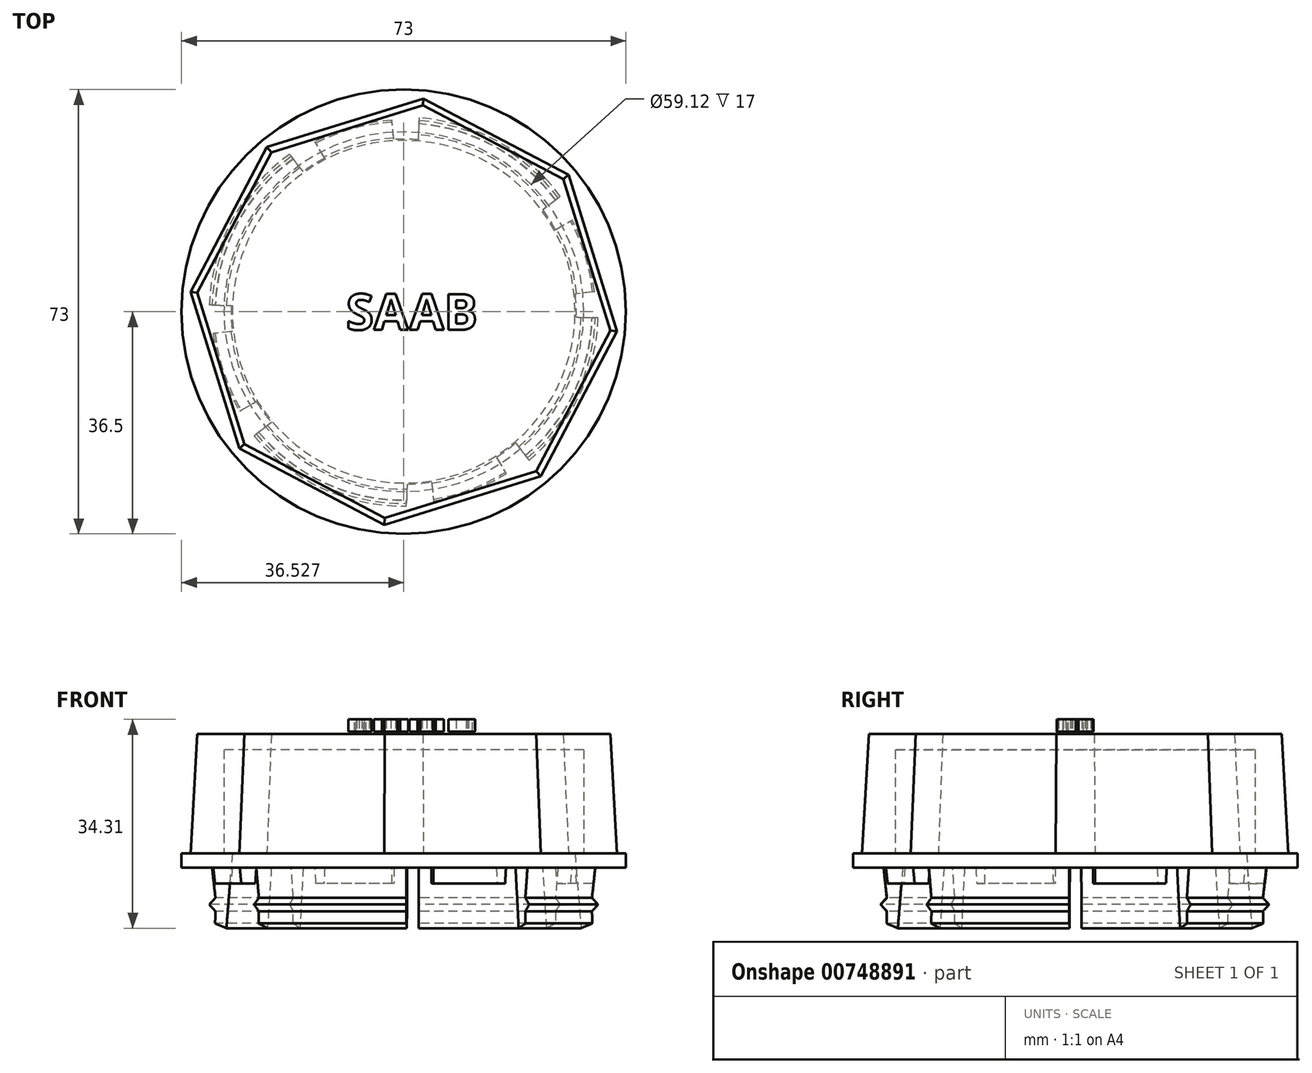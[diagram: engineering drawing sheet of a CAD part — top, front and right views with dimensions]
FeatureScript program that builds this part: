
annotation { "Feature Type Name" : "Feature", "Feature Type Description" : "" }
export const myFeature = defineFeature(function(context is Context, id is Id, definition is map)
    precondition{}
    {
        {
            var Q0;
            Q0=qCreatedBy(makeId("Top.planeOp"),FACE);
            var sketch = newSketch(context, id + "F0", { "sketchPlane" : qUnion([Q0])});
            skCircle(sketch, "E0.cCircle", {"center": v(41.88, 0) * mm, "radius": 35.18 * mm, "construction": true});
            skLineSegment(sketch, "E0.0", {"start": v(14.82, -22.49) * mm, "end": v(6.85, 3.23) * mm});
            skLineSegment(sketch, "E0.1", {"start": v(6.85, 3.23) * mm, "end": v(19.39, 27.05) * mm});
            skLineSegment(sketch, "E0.2", {"start": v(19.39, 27.05) * mm, "end": v(45.1, 35.03) * mm});
            skLineSegment(sketch, "E0.3", {"start": v(45.1, 35.03) * mm, "end": v(68.93, 22.49) * mm});
            skLineSegment(sketch, "E0.4", {"start": v(68.93, 22.49) * mm, "end": v(76.9, -3.23) * mm});
            skLineSegment(sketch, "E0.5", {"start": v(76.9, -3.23) * mm, "end": v(64.36, -27.05) * mm});
            skLineSegment(sketch, "E0.6", {"start": v(64.36, -27.05) * mm, "end": v(38.65, -35.03) * mm});
            skLineSegment(sketch, "E0.7", {"start": v(38.65, -35.03) * mm, "end": v(14.82, -22.49) * mm});
            skSolve(sketch);
        }
        {
            var Q0;
            Q0=qSketchRegion(id+"F0",true);
            extrude(context, id + "F1", {"entities" : qUnion([Q0]), "depth" : 19.6 * mm, "offsetDistance" : 25 * mm, "hasDraft" : true, "draftAngle" : 3 * degree, "draftPullDirection" : true});
        }
        {
            var Q0;
            Q0=qCreatedBy(makeId("Front.planeOp"),FACE);
            var sketch = newSketch(context, id + "F2", { "sketchPlane" : qUnion([Q0])});
            skLineSegment(sketch, "E1", {"start": v(71.3, 19.61) * mm, "end": v(71.3, 20.31) * mm});
            skLineSegment(sketch, "E2", {"start": v(71.3, 20.31) * mm, "end": v(70.7, 20.31) * mm});
            skLineSegment(sketch, "E3", {"start": v(70.7, 20.31) * mm, "end": v(70.7, 19.61) * mm});
            skLineSegment(sketch, "E4", {"start": v(61.4, 22) * mm, "end": v(61.4, 21.36) * mm});
            skLineSegment(sketch, "E5", {"start": v(61.4, 21.36) * mm, "end": v(41.94, 21.36) * mm});
            skArc(sketch, "E6", {"start": v(70.7, 19.61) * mm, "mid": v(66.19, 21.38) * mm, "end": v(61.4, 22) * mm});
            skLineSegment(sketch, "E7", {"start": v(41.94, 21.36) * mm, "end": v(41.94, 19.6) * mm});
            skSolve(sketch);
        }
        {
            var Q0;
            Q0=qSketchRegion(id+"F2",true);
            var Q1;
            Q1=sQuery(id+"F2.wireOp",EDGE,"E5");
            var Q2;
            Q2=sQuery(id+"F2.wireOp",EDGE,"E4");
            var Q3;
            Q3=sQuery(id+"F2.wireOp",EDGE,"E6");
            var Q4;
            Q4=sQuery(id+"F2.wireOp",EDGE,"E1");
            var Q5;
            Q5=sQuery(id+"F2.wireOp",EDGE,"E3");
            var Q6;
            Q6=sQuery(id+"F2.wireOp",EDGE,"E2");
            var Q7;
            Q7=sQuery(id+"F2.wireOp",EDGE,"E7");
            revolve(context, id + "F3", {"bodyType" : ToolBodyType.SURFACE, "surfaceOperationType" : NewSurfaceOperationType.NEW, "entities" : qUnion([Q0]), "surfaceEntities" : qUnion([Q1, Q2, Q3, Q4, Q5, Q6]), "axis" : qUnion([Q7]), "revolveType" : RevolveType.FULL});
        }
        {
            var Q0;
            Q0=qCreatedBy(makeId("Front.planeOp"),FACE);
            var sketch = newSketch(context, id + "F4", { "sketchPlane" : qUnion([Q0])});
            skLineSegment(sketch, "E8", {"start": v(41.85, 2.47) * mm, "end": v(41.85, -0.28) * mm});
            skLineSegment(sketch, "E9", {"start": v(13.92, 0) * mm, "end": v(10.66, 0) * mm});
            skLineSegment(sketch, "E10", {"start": v(13.7, 0) * mm, "end": v(12.7, -12.3) * mm});
            skLineSegment(sketch, "E11", {"start": v(12.7, -12.3) * mm, "end": v(10.85, -11.54) * mm});
            skLineSegment(sketch, "E12", {"start": v(10.85, -11.54) * mm, "end": v(10.9, -9.54) * mm});
            skLineSegment(sketch, "E13", {"start": v(9.9, -8.43) * mm, "end": v(10.9, -9.54) * mm});
            skLineSegment(sketch, "E14", {"start": v(9.9, -8.43) * mm, "end": v(10.9, -7.32) * mm});
            skLineSegment(sketch, "E15", {"start": v(10.9, -7.32) * mm, "end": v(10.35, -2.35) * mm});
            skLineSegment(sketch, "E16", {"start": v(41.85, 0) * mm, "end": v(5.35, 0) * mm});
            skLineSegment(sketch, "E17", {"start": v(41.85, 2.47) * mm, "end": v(41.85, -22.81) * mm});
            skPoint(sketch, "E18", {"position": v(5.35, -2.35) * mm});
            skLineSegment(sketch, "E19", {"start": v(5.35, -2.35) * mm, "end": v(10.35, -2.35) * mm});
            skLineSegment(sketch, "E20", {"start": v(5.35, 0) * mm, "end": v(5.35, -2.35) * mm});
            skPoint(sketch, "E21", {"position": v(10.85, 0) * mm});
            skSolve(sketch);
        }
        {
            var Q0;
            Q0=qSketchRegion(id+"F4",true);
            var Q1;
            Q1=sQuery(id+"F4.wireOp",EDGE,"E16");
            var Q2;
            Q2=sQuery(id+"F4.wireOp",EDGE,"4cd7ZZWE-5ar5-vtm7-FDXw-HXyrbe5Stu3w");
            var Q3;
            Q3=sQuery(id+"F4.wireOp",EDGE,"E15");
            var Q4;
            Q4=sQuery(id+"F4.wireOp",EDGE,"E14");
            var Q5;
            Q5=sQuery(id+"F4.wireOp",EDGE,"E13");
            var Q6;
            Q6=sQuery(id+"F4.wireOp",EDGE,"E11");
            var Q7;
            Q7=sQuery(id+"F4.wireOp",EDGE,"E12");
            var Q8;
            Q8=sQuery(id+"F4.wireOp",EDGE,"E10");
            var Q9;
            Q9=sQuery(id+"F4.wireOp",EDGE,"E17");
            revolve(context, id + "F5", {"surfaceOperationType" : NewSurfaceOperationType.NEW, "entities" : qUnion([Q0]), "surfaceEntities" : qUnion([Q1, Q2, Q3, Q4, Q5, Q6, Q7, Q8]), "axis" : qUnion([Q9]), "revolveType" : RevolveType.FULL});
        }
        {
            var Q0;
            Q0=qCreatedBy(makeId("Top.planeOp"),FACE);
            var sketch = newSketch(context, id + "F6", { "sketchPlane" : qUnion([Q0])});
            skCircle(sketch, "E22", {"center": v(41.88, 0) * mm, "radius": 29.56 * mm});
            skSolve(sketch);
        }
        {
            var Q0;
            Q0=qSketchRegion(id+"F6",true);
            extrude(context, id + "F7", {"entities" : qUnion([Q0]), "operationType" : NewBodyOperationType.REMOVE, "depth" : 17 * mm, "offsetDistance" : 25 * mm});
        }
        {
            var Q0;
            Q0=qCreatedBy(makeId("Top.planeOp"),FACE);
            var sketch = newSketch(context, id + "F8", { "sketchPlane" : qUnion([Q0])});
            skText(sketch, "E23", { "text": "SAAB", "fontName": "OpenSans-Bold.ttf"});
            const initialGuessF8  = {"E23": [0.03239, -0.00298, 1, 0, 0.00593]};
            skSetInitialGuess(sketch, initialGuessF8);
            skSolve(sketch);
        }
        {
            var Q0;
            Q0=qSketchRegion(id+"F8",true);
            extrude(context, id + "F9", {"entities" : qUnion([Q0]), "depth" : 2 * mm, "offsetDistance" : 25 * mm});
        }
        {
            var Q0;
            Q0=makeQuery(id+"F9.opExtrude","SWEPT_BODY",BODY,{"disambiguationData":[OSD([sQuery(id+"F8.wireOp",EDGE,"E23.sketch_text.stroke-0"),sQuery(id+"F8.wireOp",EDGE,"E23.sketch_text.stroke-1"),sQuery(id+"F8.wireOp",EDGE,"E23.sketch_text.stroke-2"),sQuery(id+"F8.wireOp",EDGE,"E23.sketch_text.stroke-3"),sQuery(id+"F8.wireOp",EDGE,"E23.sketch_text.stroke-4"),sQuery(id+"F8.wireOp",EDGE,"E23.sketch_text.stroke-5"),sQuery(id+"F8.wireOp",EDGE,"E23.sketch_text.stroke-6"),sQuery(id+"F8.wireOp",EDGE,"E23.sketch_text.stroke-7"),sQuery(id+"F8.wireOp",EDGE,"E23.sketch_text.stroke-8"),sQuery(id+"F8.wireOp",EDGE,"E23.sketch_text.stroke-9"),sQuery(id+"F8.wireOp",EDGE,"E23.sketch_text.stroke-10"),sQuery(id+"F8.wireOp",EDGE,"E23.sketch_text.stroke-11"),sQuery(id+"F8.wireOp",EDGE,"E23.sketch_text.stroke-12"),sQuery(id+"F8.wireOp",EDGE,"E23.sketch_text.stroke-13"),sQuery(id+"F8.wireOp",EDGE,"E23.sketch_text.stroke-14"),sQuery(id+"F8.wireOp",EDGE,"E23.sketch_text.stroke-15"),sQuery(id+"F8.wireOp",EDGE,"E23.sketch_text.stroke-16"),sQuery(id+"F8.wireOp",EDGE,"E23.sketch_text.stroke-17"),sQuery(id+"F8.wireOp",EDGE,"E23.sketch_text.stroke-18"),sQuery(id+"F8.wireOp",EDGE,"E23.sketch_text.stroke-19"),sQuery(id+"F8.wireOp",EDGE,"E23.sketch_text.stroke-20"),sQuery(id+"F8.wireOp",EDGE,"E23.sketch_text.stroke-21"),sQuery(id+"F8.wireOp",EDGE,"E23.sketch_text.stroke-22"),sQuery(id+"F8.wireOp",EDGE,"E23.sketch_text.stroke-23"),sQuery(id+"F8.wireOp",EDGE,"E23.sketch_text.stroke-24"),sQuery(id+"F8.wireOp",EDGE,"E23.sketch_text.stroke-25"),sQuery(id+"F8.wireOp",EDGE,"E23.sketch_text.stroke-26"),sQuery(id+"F8.wireOp",EDGE,"E23.sketch_text.stroke-27")])]});
            var Q1;
            Q1=makeQuery(id+"F9.opExtrude","SWEPT_BODY",BODY,{"disambiguationData":[OSD([sQuery(id+"F8.wireOp",EDGE,"E23.sketch_text.stroke-28"),sQuery(id+"F8.wireOp",EDGE,"E23.sketch_text.stroke-29"),sQuery(id+"F8.wireOp",EDGE,"E23.sketch_text.stroke-30"),sQuery(id+"F8.wireOp",EDGE,"E23.sketch_text.stroke-31"),sQuery(id+"F8.wireOp",EDGE,"E23.sketch_text.stroke-32"),sQuery(id+"F8.wireOp",EDGE,"E23.sketch_text.stroke-33"),sQuery(id+"F8.wireOp",EDGE,"E23.sketch_text.stroke-34"),sQuery(id+"F8.wireOp",EDGE,"E23.sketch_text.stroke-35"),sQuery(id+"F8.wireOp",EDGE,"E23.sketch_text.stroke-36"),sQuery(id+"F8.wireOp",EDGE,"E23.sketch_text.stroke-37"),sQuery(id+"F8.wireOp",EDGE,"E23.sketch_text.stroke-38"),sQuery(id+"F8.wireOp",EDGE,"E23.sketch_text.stroke-39")])]});
            var Q2;
            Q2=makeQuery(id+"F9.opExtrude","SWEPT_BODY",BODY,{"disambiguationData":[OSD([sQuery(id+"F8.wireOp",EDGE,"E23.sketch_text.stroke-40"),sQuery(id+"F8.wireOp",EDGE,"E23.sketch_text.stroke-41"),sQuery(id+"F8.wireOp",EDGE,"E23.sketch_text.stroke-42"),sQuery(id+"F8.wireOp",EDGE,"E23.sketch_text.stroke-43"),sQuery(id+"F8.wireOp",EDGE,"E23.sketch_text.stroke-44"),sQuery(id+"F8.wireOp",EDGE,"E23.sketch_text.stroke-45"),sQuery(id+"F8.wireOp",EDGE,"E23.sketch_text.stroke-46"),sQuery(id+"F8.wireOp",EDGE,"E23.sketch_text.stroke-47"),sQuery(id+"F8.wireOp",EDGE,"E23.sketch_text.stroke-48"),sQuery(id+"F8.wireOp",EDGE,"E23.sketch_text.stroke-49"),sQuery(id+"F8.wireOp",EDGE,"E23.sketch_text.stroke-50"),sQuery(id+"F8.wireOp",EDGE,"E23.sketch_text.stroke-51")])]});
            var Q3;
            Q3=makeQuery(id+"F9.opExtrude","SWEPT_BODY",BODY,{"disambiguationData":[OSD([sQuery(id+"F8.wireOp",EDGE,"E23.sketch_text.stroke-52"),sQuery(id+"F8.wireOp",EDGE,"E23.sketch_text.stroke-53"),sQuery(id+"F8.wireOp",EDGE,"E23.sketch_text.stroke-54"),sQuery(id+"F8.wireOp",EDGE,"E23.sketch_text.stroke-55"),sQuery(id+"F8.wireOp",EDGE,"E23.sketch_text.stroke-56"),sQuery(id+"F8.wireOp",EDGE,"E23.sketch_text.stroke-57"),sQuery(id+"F8.wireOp",EDGE,"E23.sketch_text.stroke-58"),sQuery(id+"F8.wireOp",EDGE,"E23.sketch_text.stroke-59"),sQuery(id+"F8.wireOp",EDGE,"E23.sketch_text.stroke-60"),sQuery(id+"F8.wireOp",EDGE,"E23.sketch_text.stroke-61"),sQuery(id+"F8.wireOp",EDGE,"E23.sketch_text.stroke-62"),sQuery(id+"F8.wireOp",EDGE,"E23.sketch_text.stroke-63"),sQuery(id+"F8.wireOp",EDGE,"E23.sketch_text.stroke-64"),sQuery(id+"F8.wireOp",EDGE,"E23.sketch_text.stroke-65"),sQuery(id+"F8.wireOp",EDGE,"E23.sketch_text.stroke-66"),sQuery(id+"F8.wireOp",EDGE,"E23.sketch_text.stroke-67"),sQuery(id+"F8.wireOp",EDGE,"E23.sketch_text.stroke-68"),sQuery(id+"F8.wireOp",EDGE,"E23.sketch_text.stroke-69"),sQuery(id+"F8.wireOp",EDGE,"E23.sketch_text.stroke-70"),sQuery(id+"F8.wireOp",EDGE,"E23.sketch_text.stroke-71"),sQuery(id+"F8.wireOp",EDGE,"E23.sketch_text.stroke-72"),sQuery(id+"F8.wireOp",EDGE,"E23.sketch_text.stroke-73"),sQuery(id+"F8.wireOp",EDGE,"E23.sketch_text.stroke-74"),sQuery(id+"F8.wireOp",EDGE,"E23.sketch_text.stroke-75"),sQuery(id+"F8.wireOp",EDGE,"E23.sketch_text.stroke-76")])]});
            transform(context, id + "F10", {"entities" : qUnion([Q0, Q1, Q2, Q3]), "transformType" : TransformType.TRANSLATION_3D, "dx" : 0 * mm, "dy" : 0 * mm, "dz" : 20 * mm, "makeCopy" : false});
        }
        {
            var Q0;
            Q0=qCreatedBy(makeId("Top.planeOp"),FACE);
            var sketch = newSketch(context, id + "F11", { "sketchPlane" : qUnion([Q0])});
            skLineSegment(sketch, "E24", {"start": v(69.85, -34.13) * mm, "end": v(16.32, 34.78) * mm});
            skLineSegment(sketch, "E25", {"start": v(16.32, 34.78) * mm, "end": v(43.91, 43.26) * mm});
            skLineSegment(sketch, "E26", {"start": v(43.91, 43.26) * mm, "end": v(42.61, -43.16) * mm});
            skLineSegment(sketch, "E27", {"start": v(9.14, -26.59) * mm, "end": v(79.03, 27.7) * mm});
            skLineSegment(sketch, "E28", {"start": v(79.03, 27.7) * mm, "end": v(86.57, -0.61) * mm});
            skLineSegment(sketch, "E29", {"start": v(86.57, -0.61) * mm, "end": v(43.22, 0) * mm});
            skLineSegment(sketch, "E30", {"start": v(42.61, -43.16) * mm, "end": v(69.85, -34.13) * mm});
            skLineSegment(sketch, "E31", {"start": v(0, 0.68) * mm, "end": v(43.22, 0) * mm});
            skLineSegment(sketch, "E32", {"start": v(9.14, -26.59) * mm, "end": v(0, 0.68) * mm});
            skPoint(sketch, "E33", {"position": v(19.48, -18.55) * mm});
            skPoint(sketch, "E34", {"position": v(12.6, 0.48) * mm});
            skPoint(sketch, "E35", {"position": v(24.83, 23.83) * mm});
            skPoint(sketch, "E36", {"position": v(42.83, -28.88) * mm});
            skPoint(sketch, "E37", {"position": v(60.43, -22) * mm});
            skPoint(sketch, "E38", {"position": v(71.17, -0.4) * mm});
            skPoint(sketch, "E39", {"position": v(65.22, 16.98) * mm});
            skPoint(sketch, "E40", {"position": v(43.69, 28.4) * mm});
            skLineSegment(sketch, "E41", {"start": v(12.6, 0.48) * mm, "end": v(19.48, -18.55) * mm});
            skLineSegment(sketch, "E42", {"start": v(24.83, 23.83) * mm, "end": v(43.69, 28.4) * mm});
            skLineSegment(sketch, "E43", {"start": v(65.22, 16.98) * mm, "end": v(71.17, -0.4) * mm});
            skLineSegment(sketch, "E44", {"start": v(60.43, -22) * mm, "end": v(42.83, -28.88) * mm});
            skSolve(sketch);
        }
        {
            var Q0;
            Q0 = qSketchRegion(id + "F11", true);
            extrude(context, id + "F12", {"entities" : qUnion([Q0]), "oppositeDirection" : true, "depth" : 25 * mm, "offsetDistance" : 25 * mm, "hasSecondDirection" : true, "secondDirectionOppositeDirection" : true, "secondDirectionDepth" : 5 * mm});
        }
        {
            var Q0;
            Q0=makeQuery(id+"F12.opExtrude","SWEPT_BODY",BODY,{"disambiguationData":[OSD([sQuery(id+"F11.wireOp",EDGE,"E24"),sQuery(id+"F11.wireOp",EDGE,"E26"),sQuery(id+"F11.wireOp",EDGE,"E27"),sQuery(id+"F11.wireOp",EDGE,"E29"),sQuery(id+"F11.wireOp",EDGE,"E30"),sQuery(id+"F11.wireOp",EDGE,"E31"),sQuery(id+"F11.wireOp",EDGE,"E32")])]});
            var Q1;
            Q1=makeQuery(id+"F12.opExtrude","SWEPT_BODY",BODY,{"disambiguationData":[OSD([sQuery(id+"F11.wireOp",EDGE,"E27"),sQuery(id+"F11.wireOp",EDGE,"E28"),sQuery(id+"F11.wireOp",EDGE,"E29")])]});
            var Q2;
            Q2=makeQuery(id+"F12.opExtrude","SWEPT_BODY",BODY,{"disambiguationData":[OSD([sQuery(id+"F11.wireOp",EDGE,"E24"),sQuery(id+"F11.wireOp",EDGE,"E25"),sQuery(id+"F11.wireOp",EDGE,"E26")])]});
            var Q3;
            Q3=makeQuery(id+"FadKjfFnsJpzDV8_9.opBoolean","SPLIT",BODY,{"disambiguationData":[OD(5.0)],"derivedFrom":makeQuery(id+"F5.opRevolve","SWEPT_BODY",BODY,{"disambiguationData":[OSD([sQuery(id+"F4.wireOp",EDGE,"E10"),sQuery(id+"F4.wireOp",EDGE,"E11"),sQuery(id+"F4.wireOp",EDGE,"E12"),sQuery(id+"F4.wireOp",EDGE,"E13"),sQuery(id+"F4.wireOp",EDGE,"E14"),sQuery(id+"F4.wireOp",EDGE,"E15"),sQuery(id+"F4.wireOp",EDGE,"E16"),sQuery(id+"F4.wireOp",EDGE,"E19"),sQuery(id+"F4.wireOp",EDGE,"E20")])]})});
            var Q4;
            Q4=makeQuery(id+"FadKjfFnsJpzDV8_9.opBoolean","SPLIT",BODY,{"disambiguationData":[OD(3.0)],"derivedFrom":makeQuery(id+"F5.opRevolve","SWEPT_BODY",BODY,{"disambiguationData":[OSD([sQuery(id+"F4.wireOp",EDGE,"E10"),sQuery(id+"F4.wireOp",EDGE,"E11"),sQuery(id+"F4.wireOp",EDGE,"E12"),sQuery(id+"F4.wireOp",EDGE,"E13"),sQuery(id+"F4.wireOp",EDGE,"E14"),sQuery(id+"F4.wireOp",EDGE,"E15"),sQuery(id+"F4.wireOp",EDGE,"E16"),sQuery(id+"F4.wireOp",EDGE,"E19"),sQuery(id+"F4.wireOp",EDGE,"E20")])]})});
            var Q5;
            Q5=makeQuery(id+"FadKjfFnsJpzDV8_9.opBoolean","SPLIT",BODY,{"disambiguationData":[OD(7.0)],"derivedFrom":makeQuery(id+"F5.opRevolve","SWEPT_BODY",BODY,{"disambiguationData":[OSD([sQuery(id+"F4.wireOp",EDGE,"E10"),sQuery(id+"F4.wireOp",EDGE,"E11"),sQuery(id+"F4.wireOp",EDGE,"E12"),sQuery(id+"F4.wireOp",EDGE,"E13"),sQuery(id+"F4.wireOp",EDGE,"E14"),sQuery(id+"F4.wireOp",EDGE,"E15"),sQuery(id+"F4.wireOp",EDGE,"E16"),sQuery(id+"F4.wireOp",EDGE,"E19"),sQuery(id+"F4.wireOp",EDGE,"E20")])]})});
            var Q6;
            Q6=makeQuery(id+"FadKjfFnsJpzDV8_9.opBoolean","SPLIT",BODY,{"disambiguationData":[OD(2.0)],"derivedFrom":makeQuery(id+"F5.opRevolve","SWEPT_BODY",BODY,{"disambiguationData":[OSD([sQuery(id+"F4.wireOp",EDGE,"E10"),sQuery(id+"F4.wireOp",EDGE,"E11"),sQuery(id+"F4.wireOp",EDGE,"E12"),sQuery(id+"F4.wireOp",EDGE,"E13"),sQuery(id+"F4.wireOp",EDGE,"E14"),sQuery(id+"F4.wireOp",EDGE,"E15"),sQuery(id+"F4.wireOp",EDGE,"E16"),sQuery(id+"F4.wireOp",EDGE,"E19"),sQuery(id+"F4.wireOp",EDGE,"E20")])]})});
            var Q7;
            Q7=makeQuery(id+"FadKjfFnsJpzDV8_9.opBoolean","SPLIT",BODY,{"disambiguationData":[OD(0.0)],"derivedFrom":makeQuery(id+"F5.opRevolve","SWEPT_BODY",BODY,{"disambiguationData":[OSD([sQuery(id+"F4.wireOp",EDGE,"E10"),sQuery(id+"F4.wireOp",EDGE,"E11"),sQuery(id+"F4.wireOp",EDGE,"E12"),sQuery(id+"F4.wireOp",EDGE,"E13"),sQuery(id+"F4.wireOp",EDGE,"E14"),sQuery(id+"F4.wireOp",EDGE,"E15"),sQuery(id+"F4.wireOp",EDGE,"E16"),sQuery(id+"F4.wireOp",EDGE,"E19"),sQuery(id+"F4.wireOp",EDGE,"E20")])]})});
            var Q8;
            Q8=makeQuery(id+"FadKjfFnsJpzDV8_9.opBoolean","SPLIT",BODY,{"disambiguationData":[OD(6.0)],"derivedFrom":makeQuery(id+"F5.opRevolve","SWEPT_BODY",BODY,{"disambiguationData":[OSD([sQuery(id+"F4.wireOp",EDGE,"E10"),sQuery(id+"F4.wireOp",EDGE,"E11"),sQuery(id+"F4.wireOp",EDGE,"E12"),sQuery(id+"F4.wireOp",EDGE,"E13"),sQuery(id+"F4.wireOp",EDGE,"E14"),sQuery(id+"F4.wireOp",EDGE,"E15"),sQuery(id+"F4.wireOp",EDGE,"E16"),sQuery(id+"F4.wireOp",EDGE,"E19"),sQuery(id+"F4.wireOp",EDGE,"E20")])]})});
            var Q9;
            Q9=makeQuery(id+"FadKjfFnsJpzDV8_9.opBoolean","SPLIT",BODY,{"disambiguationData":[OD(4.0)],"derivedFrom":makeQuery(id+"F5.opRevolve","SWEPT_BODY",BODY,{"disambiguationData":[OSD([sQuery(id+"F4.wireOp",EDGE,"E10"),sQuery(id+"F4.wireOp",EDGE,"E11"),sQuery(id+"F4.wireOp",EDGE,"E12"),sQuery(id+"F4.wireOp",EDGE,"E13"),sQuery(id+"F4.wireOp",EDGE,"E14"),sQuery(id+"F4.wireOp",EDGE,"E15"),sQuery(id+"F4.wireOp",EDGE,"E16"),sQuery(id+"F4.wireOp",EDGE,"E19"),sQuery(id+"F4.wireOp",EDGE,"E20")])]})});
            var Q10;
            Q10=makeQuery(id+"FadKjfFnsJpzDV8_9.opBoolean","SPLIT",BODY,{"disambiguationData":[OD(1.0)],"derivedFrom":makeQuery(id+"F5.opRevolve","SWEPT_BODY",BODY,{"disambiguationData":[OSD([sQuery(id+"F4.wireOp",EDGE,"E10"),sQuery(id+"F4.wireOp",EDGE,"E11"),sQuery(id+"F4.wireOp",EDGE,"E12"),sQuery(id+"F4.wireOp",EDGE,"E13"),sQuery(id+"F4.wireOp",EDGE,"E14"),sQuery(id+"F4.wireOp",EDGE,"E15"),sQuery(id+"F4.wireOp",EDGE,"E16"),sQuery(id+"F4.wireOp",EDGE,"E19"),sQuery(id+"F4.wireOp",EDGE,"E20")])]})});
            booleanBodies(context, id + "F13", {"operationType" : BooleanOperationType.SUBTRACTION, "tools" : qUnion([Q0, Q1, Q2]), "targets" : qUnion([Q3, Q4, Q5, Q6, Q7, Q8, Q9, Q10])});
        }
        {
            var Q0;
            Q0=qCreatedBy(makeId("Top.planeOp"),FACE);
            var sketch = newSketch(context, id + "F14", { "sketchPlane" : qUnion([Q0])});
            skPoint(sketch, "E45.endSnap0", {"position": v(222.12, 4.24) * mm});
            skPoint(sketch, "E46", {"position": v(43.35, 0) * mm});
            skLineSegment(sketch, "E47", {"start": v(76.6, 26.03) * mm, "end": v(5.98, -29.26) * mm});
            skLineSegment(sketch, "E48", {"start": v(43.35, 0) * mm, "end": v(74.1, -39.28) * mm});
            skLineSegment(sketch, "E49", {"start": v(43.35, 0) * mm, "end": v(14.72, 36.58) * mm});
            skLineSegment(sketch, "E50", {"start": v(1.61, -23.99) * mm, "end": v(43.35, 0) * mm});
            skLineSegment(sketch, "E51", {"start": v(43.35, 0) * mm, "end": v(69.77, -45.97) * mm});
            skLineSegment(sketch, "E52", {"start": v(43.35, 0) * mm, "end": v(81.27, 21.79) * mm});
            skLineSegment(sketch, "E53", {"start": v(43.35, 0) * mm, "end": v(20.03, 40.59) * mm});
            skLineSegment(sketch, "E54", {"start": v(14.72, 36.58) * mm, "end": v(20.03, 40.59) * mm});
            skLineSegment(sketch, "E55", {"start": v(76.6, 26.03) * mm, "end": v(81.27, 21.79) * mm});
            skLineSegment(sketch, "E56", {"start": v(74.1, -39.28) * mm, "end": v(69.77, -45.97) * mm});
            skLineSegment(sketch, "E57", {"start": v(5.98, -29.26) * mm, "end": v(1.61, -23.99) * mm});
            skLineSegment(sketch, "E58", {"start": v(85.32, 4.6) * mm, "end": v(-3.82, -5.18) * mm});
            skLineSegment(sketch, "E59", {"start": v(43.35, 0) * mm, "end": v(48.8, -49.6) * mm});
            skLineSegment(sketch, "E60", {"start": v(43.35, 0) * mm, "end": v(38.29, 46.18) * mm});
            skLineSegment(sketch, "E61", {"start": v(-4.76, 1.6) * mm, "end": v(43.35, 0) * mm});
            skLineSegment(sketch, "E62", {"start": v(43.35, 0) * mm, "end": v(41.59, -52.99) * mm});
            skLineSegment(sketch, "E63", {"start": v(43.35, 0) * mm, "end": v(87.06, -1.46) * mm});
            skLineSegment(sketch, "E64", {"start": v(43.35, 0) * mm, "end": v(44.92, 46.79) * mm});
            skLineSegment(sketch, "E65", {"start": v(38.29, 46.18) * mm, "end": v(44.92, 46.79) * mm});
            skLineSegment(sketch, "E66", {"start": v(85.32, 4.6) * mm, "end": v(87.06, -1.46) * mm});
            skLineSegment(sketch, "E67", {"start": v(48.8, -49.6) * mm, "end": v(41.59, -52.99) * mm});
            skLineSegment(sketch, "E68", {"start": v(-3.82, -5.18) * mm, "end": v(-4.76, 1.6) * mm});
            skSolve(sketch);
        }
        {
            var Q0;
            Q0 = qSketchRegion(id + "F14", true);
            extrude(context, id + "F15", {"entities" : qUnion([Q0]), "oppositeDirection" : true, "depth" : 10 * mm, "offsetDistance" : 25 * mm});
        }
        {
            var Q0;
            Q0=makeQuery(id+"F15.opExtrude","SWEPT_BODY",BODY,{"disambiguationData":[OSD([sQuery(id+"F14.wireOp",EDGE,"E49"),sQuery(id+"F14.wireOp",EDGE,"E53"),sQuery(id+"F14.wireOp",EDGE,"E54")])]});
            var Q1;
            Q1=makeQuery(id+"F15.opExtrude","SWEPT_BODY",BODY,{"disambiguationData":[OSD([sQuery(id+"F14.wireOp",EDGE,"E58"),sQuery(id+"F14.wireOp",EDGE,"E61"),sQuery(id+"F14.wireOp",EDGE,"E68")])]});
            var Q2;
            Q2=makeQuery(id+"F15.opExtrude","SWEPT_BODY",BODY,{"disambiguationData":[OSD([sQuery(id+"F14.wireOp",EDGE,"E47"),sQuery(id+"F14.wireOp",EDGE,"E50"),sQuery(id+"F14.wireOp",EDGE,"E57")])]});
            var Q3;
            Q3=makeQuery(id+"F15.opExtrude","SWEPT_BODY",BODY,{"disambiguationData":[OSD([sQuery(id+"F14.wireOp",EDGE,"E59"),sQuery(id+"F14.wireOp",EDGE,"E62"),sQuery(id+"F14.wireOp",EDGE,"E67")])]});
            var Q4;
            Q4=makeQuery(id+"F15.opExtrude","SWEPT_BODY",BODY,{"disambiguationData":[OSD([sQuery(id+"F14.wireOp",EDGE,"E48"),sQuery(id+"F14.wireOp",EDGE,"E51"),sQuery(id+"F14.wireOp",EDGE,"E56")])]});
            var Q5;
            Q5=makeQuery(id+"F15.opExtrude","SWEPT_BODY",BODY,{"disambiguationData":[OSD([sQuery(id+"F14.wireOp",EDGE,"E58"),sQuery(id+"F14.wireOp",EDGE,"E63"),sQuery(id+"F14.wireOp",EDGE,"E66")])]});
            var Q6;
            Q6=makeQuery(id+"F15.opExtrude","SWEPT_BODY",BODY,{"disambiguationData":[OSD([sQuery(id+"F14.wireOp",EDGE,"E47"),sQuery(id+"F14.wireOp",EDGE,"E52"),sQuery(id+"F14.wireOp",EDGE,"E55")])]});
            var Q7;
            Q7=makeQuery(id+"F15.opExtrude","SWEPT_BODY",BODY,{"disambiguationData":[OSD([sQuery(id+"F14.wireOp",EDGE,"E60"),sQuery(id+"F14.wireOp",EDGE,"E64"),sQuery(id+"F14.wireOp",EDGE,"E65")])]});
            transform(context, id + "F16", {"entities" : qUnion([Q0, Q1, Q2, Q3, Q4, Q5, Q6, Q7]), "transformType" : TransformType.TRANSLATION_3D, "dx" : 0 * mm, "dy" : 0 * mm, "dz" : -2.35 * mm, "makeCopy" : false});
        }
        {
            var Q0;
            Q0=makeQuery(id+"F15.opExtrude","SWEPT_BODY",BODY,{"disambiguationData":[OSD([sQuery(id+"F14.wireOp",EDGE,"E49"),sQuery(id+"F14.wireOp",EDGE,"E53"),sQuery(id+"F14.wireOp",EDGE,"E54")])]});
            var Q1;
            Q1=makeQuery(id+"F15.opExtrude","SWEPT_BODY",BODY,{"disambiguationData":[OSD([sQuery(id+"F14.wireOp",EDGE,"E58"),sQuery(id+"F14.wireOp",EDGE,"E61"),sQuery(id+"F14.wireOp",EDGE,"E68")])]});
            var Q2;
            Q2=makeQuery(id+"F15.opExtrude","SWEPT_BODY",BODY,{"disambiguationData":[OSD([sQuery(id+"F14.wireOp",EDGE,"E47"),sQuery(id+"F14.wireOp",EDGE,"E50"),sQuery(id+"F14.wireOp",EDGE,"E57")])]});
            var Q3;
            Q3=makeQuery(id+"F15.opExtrude","SWEPT_BODY",BODY,{"disambiguationData":[OSD([sQuery(id+"F14.wireOp",EDGE,"E59"),sQuery(id+"F14.wireOp",EDGE,"E62"),sQuery(id+"F14.wireOp",EDGE,"E67")])]});
            var Q4;
            Q4=makeQuery(id+"F15.opExtrude","SWEPT_BODY",BODY,{"disambiguationData":[OSD([sQuery(id+"F14.wireOp",EDGE,"E48"),sQuery(id+"F14.wireOp",EDGE,"E51"),sQuery(id+"F14.wireOp",EDGE,"E56")])]});
            var Q5;
            Q5=makeQuery(id+"F15.opExtrude","SWEPT_BODY",BODY,{"disambiguationData":[OSD([sQuery(id+"F14.wireOp",EDGE,"E58"),sQuery(id+"F14.wireOp",EDGE,"E63"),sQuery(id+"F14.wireOp",EDGE,"E66")])]});
            var Q6;
            Q6=makeQuery(id+"F15.opExtrude","SWEPT_BODY",BODY,{"disambiguationData":[OSD([sQuery(id+"F14.wireOp",EDGE,"E47"),sQuery(id+"F14.wireOp",EDGE,"E52"),sQuery(id+"F14.wireOp",EDGE,"E55")])]});
            var Q7;
            Q7=makeQuery(id+"F15.opExtrude","SWEPT_BODY",BODY,{"disambiguationData":[OSD([sQuery(id+"F14.wireOp",EDGE,"E60"),sQuery(id+"F14.wireOp",EDGE,"E64"),sQuery(id+"F14.wireOp",EDGE,"E65")])]});
            var Q8;
            Q8=makeQuery(id+"F5.opRevolve","SWEPT_BODY",BODY,{"disambiguationData":[OSD([sQuery(id+"F4.wireOp",EDGE,"E10"),sQuery(id+"F4.wireOp",EDGE,"E11"),sQuery(id+"F4.wireOp",EDGE,"E12"),sQuery(id+"F4.wireOp",EDGE,"E13"),sQuery(id+"F4.wireOp",EDGE,"E14"),sQuery(id+"F4.wireOp",EDGE,"E15"),sQuery(id+"F4.wireOp",EDGE,"E16"),sQuery(id+"F4.wireOp",EDGE,"E19"),sQuery(id+"F4.wireOp",EDGE,"E20")])]});
            booleanBodies(context, id + "F17", {"operationType" : BooleanOperationType.SUBTRACTION, "tools" : qUnion([Q0, Q1, Q2, Q3, Q4, Q5, Q6, Q7]), "targets" : qUnion([Q8])});
        }
    });
